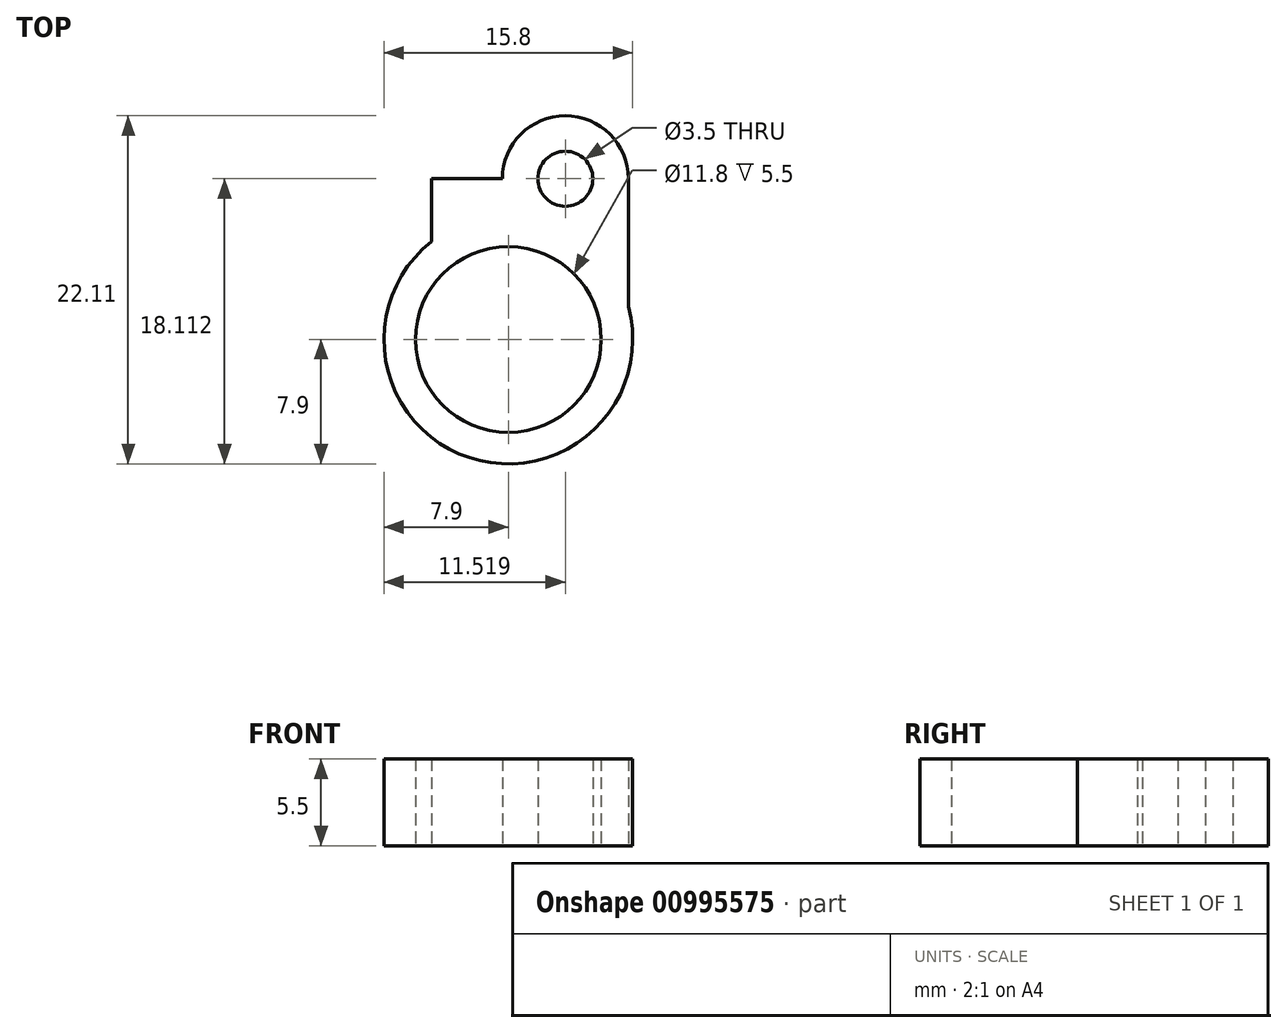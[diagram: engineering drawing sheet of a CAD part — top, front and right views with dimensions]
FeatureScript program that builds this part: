
annotation { "Feature Type Name" : "Feature", "Feature Type Description" : "" }
export const myFeature = defineFeature(function(context is Context, id is Id, definition is map)
    precondition{}
    {
        {
            var Q0;
            Q0=qCreatedBy(makeId("Top.planeOp"),FACE);
            var sketch = newSketch(context, id + "F0", { "sketchPlane" : qUnion([Q0])});
            skCircle(sketch, "E0", {"center": v(0, 0) * mm, "radius": 5.9 * mm});
            skCircle(sketch, "E1.0", {"center": v(0, 0) * mm, "radius": 7.9 * mm});
            skLineSegment(sketch, "E2", {"start": v(-4.88, 10.21) * mm, "end": v(-4.88, 6.21) * mm});
            skLineSegment(sketch, "E3", {"start": v(-4.88, 10.21) * mm, "end": v(-0.38, 10.21) * mm});
            skLineSegment(sketch, "E4", {"start": v(-0.38, 10.21) * mm, "end": v(-0.38, 14.21) * mm});
            skLineSegment(sketch, "E5", {"start": v(-0.38, 14.21) * mm, "end": v(7.62, 14.21) * mm});
            skLineSegment(sketch, "E6", {"start": v(7.62, 14.21) * mm, "end": v(7.62, 2.09) * mm});
            skLineSegment(sketch, "E7", {"start": v(-0.38, 10.21) * mm, "end": v(7.62, 10.21) * mm, "construction": true});
            skCircle(sketch, "E8", {"center": v(3.62, 10.21) * mm, "radius": 1.75 * mm});
            skSolve(sketch);
        }
        {
            var Q0;
            {var subQ0=sQuery(id+"F0.wireOp",EDGE,"E2");Q0=makeQuery(id+"F0.imprint","IMPRINT",FACE,{"disambiguationData":[TD([[makeQuery(id+"F0.imprint","IMPRINT",EDGE,{"derivedFrom":subQ0}),1.0]])]});}
            var Q1;
            Q1=makeQuery(id+"F0.imprint","IMPRINT",FACE,{"disambiguationData":[TD([[makeQuery(id+"F0.imprint","IMPRINT",EDGE,{"derivedFrom":sQuery(id+"F0.wireOp",EDGE,"E0")}),-1.0]])]});
            extrude(context, id + "F1", {"entities" : qUnion([Q0, Q1]), "depth" : 5.5 * mm, "offsetDistance" : 25 * mm});
        }
        {
            var Q0;
            Q0=makeQuery(id+"F1.opExtrude","SWEPT_EDGE",EDGE,{"disambiguationData":[OSD([sQuery(id+"F0.wireOp",EDGE,"E4"),sQuery(id+"F0.wireOp",EDGE,"E5")])]});
            var Q1;
            Q1=makeQuery(id+"F1.opExtrude","SWEPT_EDGE",EDGE,{"disambiguationData":[OSD([sQuery(id+"F0.wireOp",EDGE,"E5"),sQuery(id+"F0.wireOp",EDGE,"E6")])]});
            fillet(context, id + "F2", {"entities" : qUnion([Q0, Q1]), "radius" : 4 * mm, "tangentPropagation" : true, "allowEdgeOverflow" : false});
        }
    });
